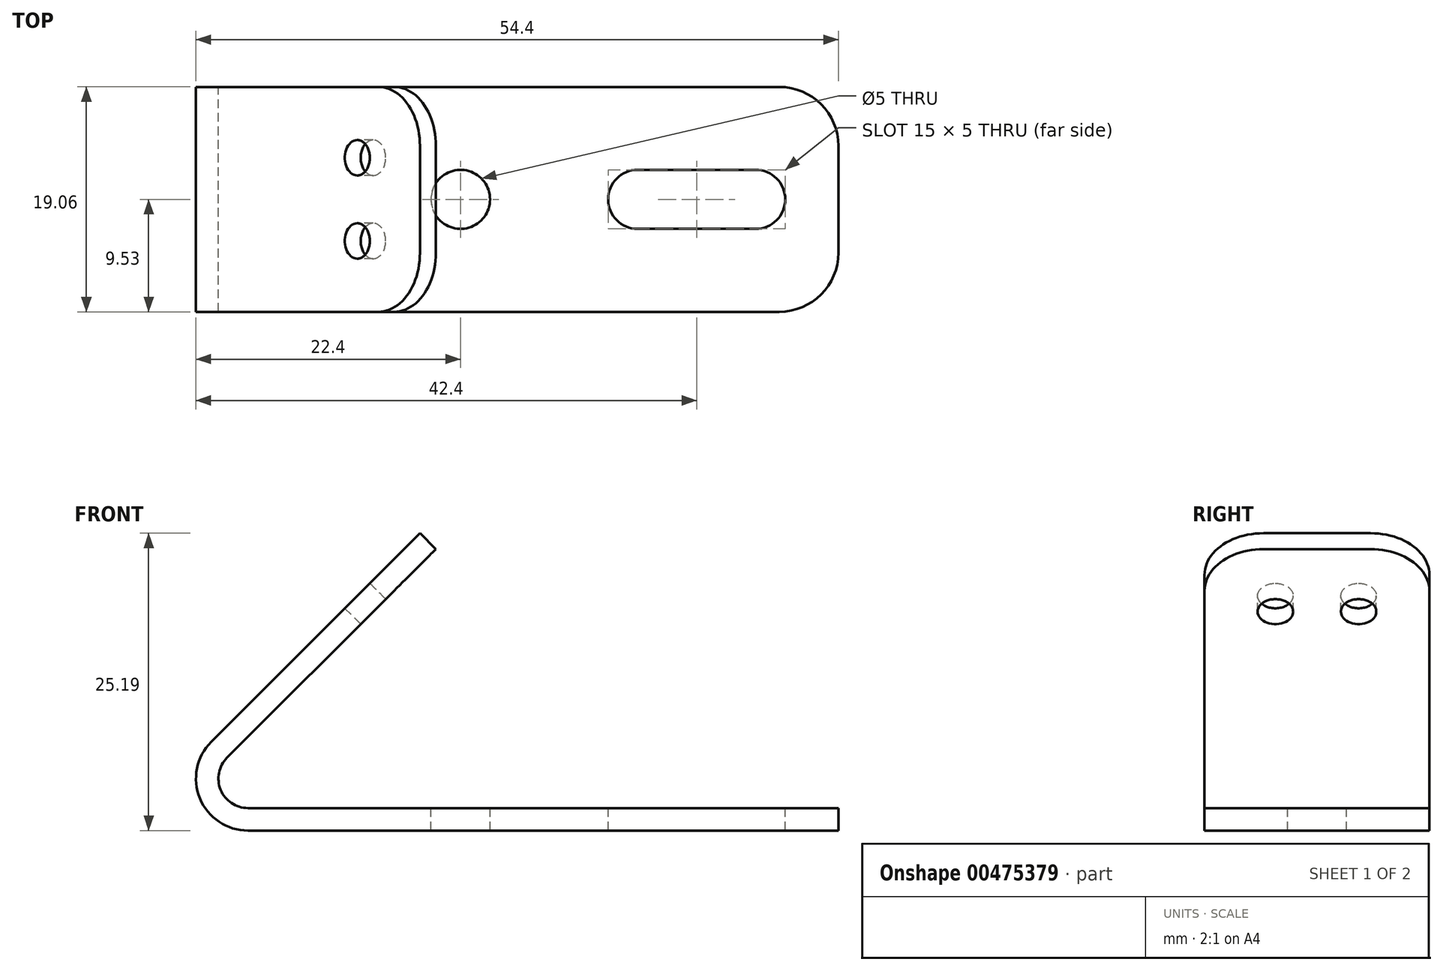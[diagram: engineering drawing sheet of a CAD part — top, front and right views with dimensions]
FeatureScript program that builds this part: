
annotation { "Feature Type Name" : "Feature", "Feature Type Description" : "" }
export const myFeature = defineFeature(function(context is Context, id is Id, definition is map)
    precondition{}
    {
        {
            var Q0;
            Q0=qCreatedBy(makeId("Front.planeOp"),FACE);
            var sketch = newSketch(context, id + "F0", { "sketchPlane" : qUnion([Q0])});
            skLineSegment(sketch, "E0", {"start": v(0, 0) * mm, "end": v(-50, 0) * mm});
            skArc(sketch, "E1", {"start": v(-50, 0) * mm, "mid": v(-54.07, 2.72) * mm, "end": v(-53.11, 7.51) * mm});
            skLineSegment(sketch, "E2", {"start": v(-53.11, 7.51) * mm, "end": v(-35.43, 25.19) * mm});
            skLineSegment(sketch, "E3.0", {"start": v(-51.77, 6.17) * mm, "end": v(-34.1, 23.85) * mm});
            skArc(sketch, "E3.1", {"start": v(-50, 1.9) * mm, "mid": v(-52.3, 3.44) * mm, "end": v(-51.77, 6.17) * mm});
            skLineSegment(sketch, "E3.2", {"start": v(0, 1.9) * mm, "end": v(-50, 1.9) * mm});
            skLineSegment(sketch, "E4", {"start": v(-34.1, 23.85) * mm, "end": v(-35.43, 25.19) * mm});
            skLineSegment(sketch, "E5", {"start": v(0, 1.9) * mm, "end": v(0, 0) * mm});
            skSolve(sketch);
        }
        {
            var Q0;
            Q0 = qSketchRegion(id + "F0", true);
            extrude(context, id + "F1", {"entities" : qUnion([Q0]), "endBound" : BoundingType.SYMMETRIC, "depth" : 19.05 * mm});
        }
        {
            var Q0;
            Q0=makeQuery(id+"F1.opExtrude","SWEPT_FACE",FACE,{"disambiguationData":[OSD([sQuery(id+"F0.wireOp",EDGE,"E3.2")])]});
            var sketch = newSketch(context, id + "F2", { "sketchPlane" : qUnion([Q0])});
            skCircle(sketch, "E6", {"center": v(-32, 0) * mm, "radius": 2.5 * mm});
            skArc(sketch, "E7", {"start": v(-17, 2.5) * mm, "mid": v(-19.5, 0) * mm, "end": v(-17, -2.5) * mm});
            skArc(sketch, "E8", {"start": v(-7, -2.5) * mm, "mid": v(-4.5, 0) * mm, "end": v(-7, 2.5) * mm});
            skLineSegment(sketch, "E9", {"start": v(-17, 2.5) * mm, "end": v(-7, 2.5) * mm});
            skLineSegment(sketch, "E10", {"start": v(-7, -2.5) * mm, "end": v(-17, -2.5) * mm});
            skLineSegment(sketch, "E11", {"start": v(0, 0) * mm, "end": v(-32, 0) * mm, "construction": true});
            skSolve(sketch);
        }
        {
            var Q0;
            Q0 = qSketchRegion(id + "F2", true);
            extrude(context, id + "F3", {"entities" : qUnion([Q0]), "operationType" : NewBodyOperationType.REMOVE, "endBound" : BoundingType.THROUGH_ALL, "oppositeDirection" : true, "depth" : 25 * mm});
        }
        {
            var Q0;
            Q0=makeQuery(id+"F1.opExtrude","SWEPT_FACE",FACE,{"disambiguationData":[OSD([sQuery(id+"F0.wireOp",EDGE,"E2")])]});
            var sketch = newSketch(context, id + "F4", { "sketchPlane" : qUnion([Q0])});
            skCircle(sketch, "E12", {"center": v(-3.53, -14.74) * mm, "radius": 1.5 * mm});
            skCircle(sketch, "E13", {"center": v(3.53, -14.74) * mm, "radius": 1.5 * mm});
            skLineSegment(sketch, "E14", {"start": v(9.53, -14.74) * mm, "end": v(-9.53, -14.74) * mm, "construction": true});
            skSolve(sketch);
        }
        {
            var Q0;
            Q0 = qSketchRegion(id + "F4", true);
            extrude(context, id + "F5", {"entities" : qUnion([Q0]), "operationType" : NewBodyOperationType.REMOVE, "endBound" : BoundingType.UP_TO_NEXT, "oppositeDirection" : true, "depth" : 25 * mm});
        }
        {
            var Q0;
            Q0=makeQuery(id+"F1.opExtrude","CAP_EDGE",EDGE,{"disambiguationData":[OSD([sQuery(id+"F0.wireOp",EDGE,"E4")])],"isStart":false});
            var Q1;
            Q1=makeQuery(id+"F1.opExtrude","CAP_EDGE",EDGE,{"disambiguationData":[OSD([sQuery(id+"F0.wireOp",EDGE,"E4")])],"isStart":true});
            var Q2;
            Q2=makeQuery(id+"F1.opExtrude","CAP_EDGE",EDGE,{"disambiguationData":[OSD([sQuery(id+"F0.wireOp",EDGE,"E5")])],"isStart":false});
            var Q3;
            Q3=makeQuery(id+"F1.opExtrude","CAP_EDGE",EDGE,{"disambiguationData":[OSD([sQuery(id+"F0.wireOp",EDGE,"E5")])],"isStart":true});
            fillet(context, id + "F6", {"entities" : qUnion([Q0, Q1, Q2, Q3]), "radius" : 5 * mm, "tangentPropagation" : true, "allowEdgeOverflow" : false});
        }
    });
